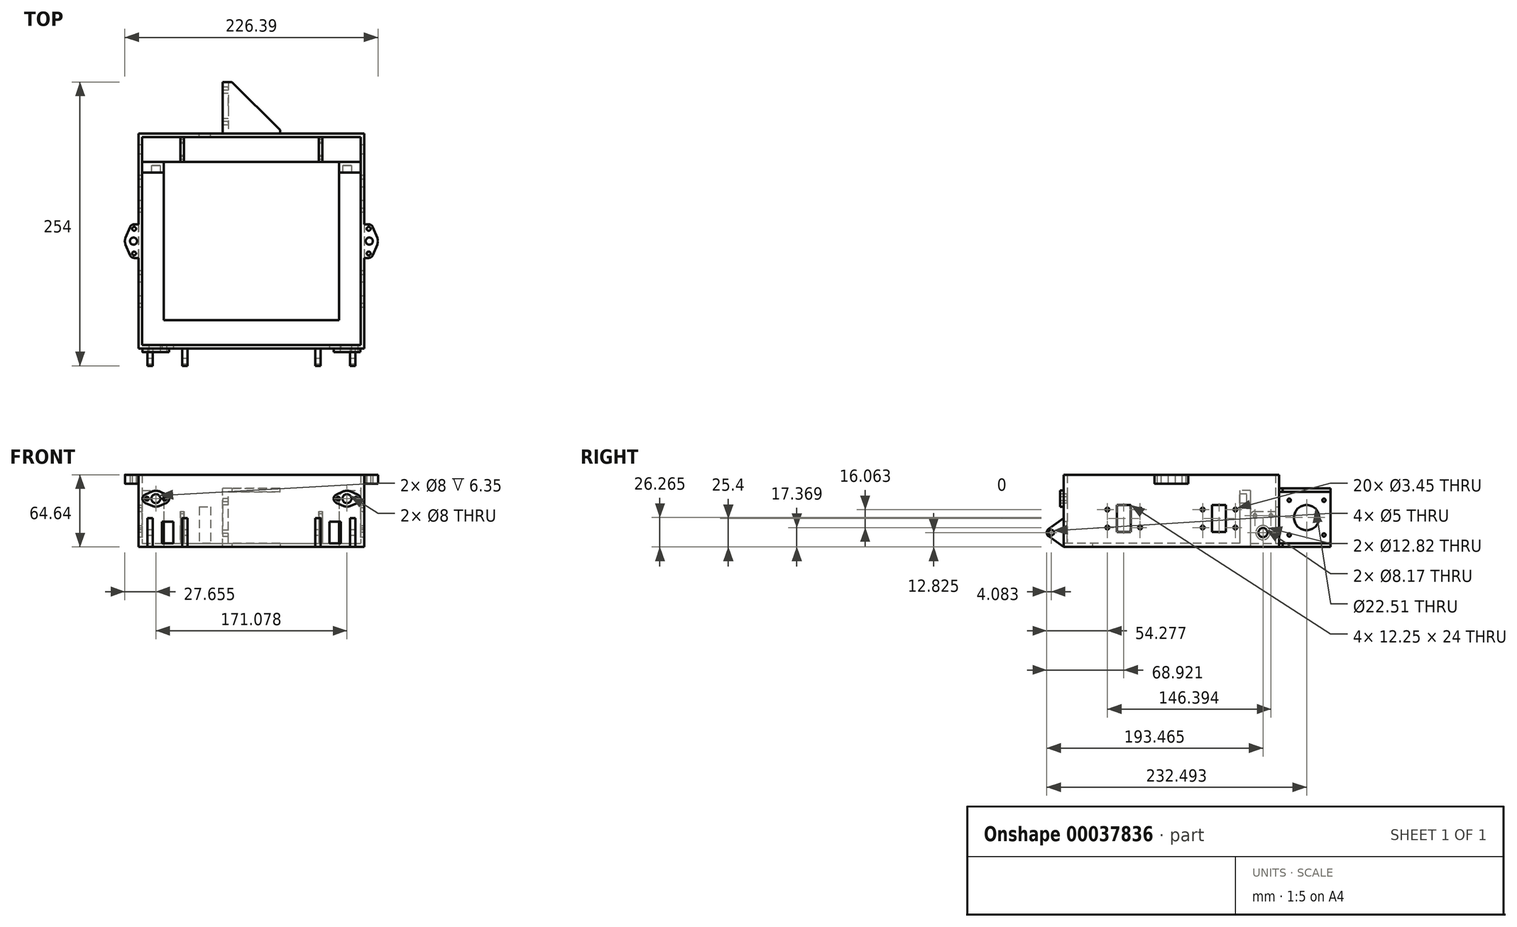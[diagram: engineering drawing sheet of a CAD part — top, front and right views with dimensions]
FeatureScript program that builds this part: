
annotation { "Feature Type Name" : "Feature", "Feature Type Description" : "" }
export const myFeature = defineFeature(function(context is Context, id is Id, definition is map)
    precondition{}
    {
        {
            var Q0;
            Q0=qCreatedBy(makeId("Top.planeOp"),FACE);
            var sketch = newSketch(context, id + "F0", { "sketchPlane" : qUnion([Q0])});
            skLineSegment(sketch, "E0.bottom", {"start": v(0, 0) * mm, "end": v(156.73, 0) * mm});
            skLineSegment(sketch, "E0.top", {"start": v(0, -141.5) * mm, "end": v(156.73, -141.5) * mm});
            skLineSegment(sketch, "E0.left", {"start": v(0, 0) * mm, "end": v(0, -141.5) * mm});
            skLineSegment(sketch, "E0.right", {"start": v(156.73, 0) * mm, "end": v(156.73, -141.5) * mm});
            skLineSegment(sketch, "E1.bottom", {"start": v(-22.61, 25.52) * mm, "end": v(179.34, 25.52) * mm});
            skLineSegment(sketch, "E1.top", {"start": v(-22.61, -167.03) * mm, "end": v(179.34, -167.03) * mm});
            skLineSegment(sketch, "E1.left", {"start": v(-22.61, 25.52) * mm, "end": v(-22.61, -167.03) * mm});
            skLineSegment(sketch, "E1.right", {"start": v(179.34, 25.52) * mm, "end": v(179.34, -167.03) * mm});
            skLineSegment(sketch, "E2", {"start": v(78.36, 0) * mm, "end": v(78.36, 25.52) * mm, "construction": true});
            skLineSegment(sketch, "E3", {"start": v(78.36, -167.03) * mm, "end": v(78.36, -141.5) * mm, "construction": true});
            skSolve(sketch);
        }
        {
            var Q0;
            Q0=qSketchRegion(id+"F0",true);
            extrude(context, id + "F1", {"entities" : qUnion([Q0]), "depth" : 3.17 * mm});
        }
        {
            var Q0;
            Q0=makeQuery(id+"F1.opExtrude","CAP_FACE",FACE,{"disambiguationData":[OSD([sQuery(id+"F0.wireOp",EDGE,"E0.bottom"),sQuery(id+"F0.wireOp",EDGE,"E0.top"),sQuery(id+"F0.wireOp",EDGE,"E0.left"),sQuery(id+"F0.wireOp",EDGE,"E0.right"),sQuery(id+"F0.wireOp",EDGE,"E1.bottom"),sQuery(id+"F0.wireOp",EDGE,"E1.top"),sQuery(id+"F0.wireOp",EDGE,"E1.left"),sQuery(id+"F0.wireOp",EDGE,"E1.right")])],"isStart":false});
            var sketch = newSketch(context, id + "F2", { "sketchPlane" : qUnion([Q0])});
            skLineSegment(sketch, "E4.bottom", {"start": v(-22.61, 25.52) * mm, "end": v(179.34, 25.52) * mm});
            skLineSegment(sketch, "E4.top", {"start": v(-22.61, -167.03) * mm, "end": v(179.34, -167.03) * mm});
            skLineSegment(sketch, "E4.left", {"start": v(-22.61, 25.52) * mm, "end": v(-22.61, -167.03) * mm});
            skLineSegment(sketch, "E4.right", {"start": v(179.34, 25.52) * mm, "end": v(179.34, -167.03) * mm});
            skLineSegment(sketch, "E5", {"start": v(78.36, 0) * mm, "end": v(78.36, -141.5) * mm, "construction": true});
            skLineSegment(sketch, "E6.rect.bottom", {"start": v(-19.44, 22.35) * mm, "end": v(176.17, 22.35) * mm});
            skLineSegment(sketch, "E6.rect.top", {"start": v(-19.44, -163.86) * mm, "end": v(176.17, -163.86) * mm});
            skLineSegment(sketch, "E6.rect.left", {"start": v(-19.44, 22.35) * mm, "end": v(-19.44, -163.86) * mm});
            skLineSegment(sketch, "E6.rect.right", {"start": v(176.17, 22.35) * mm, "end": v(176.17, -163.86) * mm});
            skPoint(sketch, "E6.rect.middle", {"position": v(78.36, -70.75) * mm});
            skLineSegment(sketch, "E7", {"start": v(-19.44, 22.35) * mm, "end": v(-22.61, 22.35) * mm, "construction": true});
            skLineSegment(sketch, "E8", {"start": v(-19.44, 22.35) * mm, "end": v(-19.44, 25.52) * mm, "construction": true});
            skSolve(sketch);
        }
        {
            var Q0;
            Q0=qSketchRegion(id+"F2",true);
            extrude(context, id + "F3", {"entities" : qUnion([Q0]), "operationType" : NewBodyOperationType.ADD, "depth" : 61.46 * mm});
        }
        {
            var Q0;
            Q0=makeQuery(id+"F1.opExtrude","CAP_FACE",FACE,{"disambiguationData":[OSD([sQuery(id+"F0.wireOp",EDGE,"E0.bottom"),sQuery(id+"F0.wireOp",EDGE,"E0.top"),sQuery(id+"F0.wireOp",EDGE,"E0.left"),sQuery(id+"F0.wireOp",EDGE,"E0.right"),sQuery(id+"F0.wireOp",EDGE,"E1.bottom"),sQuery(id+"F0.wireOp",EDGE,"E1.top"),sQuery(id+"F0.wireOp",EDGE,"E1.left"),sQuery(id+"F0.wireOp",EDGE,"E1.right")])],"isStart":false});
            var sketch = newSketch(context, id + "F4", { "sketchPlane" : qUnion([Q0])});
            skLineSegment(sketch, "E9.bottom", {"start": v(-19.44, -9.52) * mm, "end": v(0, -9.52) * mm});
            skLineSegment(sketch, "E9.top", {"start": v(-19.44, 0) * mm, "end": v(0, 0) * mm});
            skLineSegment(sketch, "E9.left", {"start": v(-19.44, -9.53) * mm, "end": v(-19.44, 0) * mm});
            skLineSegment(sketch, "E9.right", {"start": v(0, -9.52) * mm, "end": v(0, 0) * mm});
            skLineSegment(sketch, "E10.bottom", {"start": v(156.73, -9.52) * mm, "end": v(176.17, -9.52) * mm});
            skLineSegment(sketch, "E10.top", {"start": v(156.73, 0) * mm, "end": v(176.17, 0) * mm});
            skLineSegment(sketch, "E10.left", {"start": v(156.73, -9.53) * mm, "end": v(156.73, 0) * mm});
            skLineSegment(sketch, "E10.right", {"start": v(176.17, -9.53) * mm, "end": v(176.17, 0) * mm});
            skSolve(sketch);
        }
        {
            var Q0;
            Q0=qSketchRegion(id+"F4",true);
            var Q1;
            Q1=makeQuery(id+"F3.opExtrude","CAP_FACE",FACE,{"disambiguationData":[OSD([sQuery(id+"F2.wireOp",EDGE,"E4.bottom"),sQuery(id+"F2.wireOp",EDGE,"E4.top"),sQuery(id+"F2.wireOp",EDGE,"E4.left"),sQuery(id+"F2.wireOp",EDGE,"E4.right"),sQuery(id+"F2.wireOp",EDGE,"E6.rect.bottom"),sQuery(id+"F2.wireOp",EDGE,"E6.rect.top"),sQuery(id+"F2.wireOp",EDGE,"E6.rect.left"),sQuery(id+"F2.wireOp",EDGE,"E6.rect.right")])],"isStart":false});
            extrude(context, id + "F5", {"entities" : qUnion([Q0]), "operationType" : NewBodyOperationType.ADD, "endBoundEntityFace" : qUnion([Q1]), "depth" : 47.22 * mm});
        }
        {
            var Q0;
            Q0=makeQuery(id+"F5.opExtrude","SWEPT_FACE",FACE,{"disambiguationData":[OSD([sQuery(id+"F4.wireOp",EDGE,"E9.bottom")])]});
            var sketch = newSketch(context, id + "F6", { "sketchPlane" : qUnion([Q0])});
            skLineSegment(sketch, "E11.bottom", {"start": v(0, 43.22) * mm, "end": v(-7.18, 43.22) * mm, "construction": true});
            skLineSegment(sketch, "E11.right", {"start": v(-7.18, 43.22) * mm, "end": v(-7.18, 50.4) * mm, "construction": true});
            skLineSegment(sketch, "E12", {"start": v(156.73, 43.22) * mm, "end": v(163.9, 43.22) * mm, "construction": true});
            skCircle(sketch, "E13", {"center": v(163.9, 43.22) * mm, "radius": 4 * mm});
            skCircle(sketch, "E14", {"center": v(-7.18, 43.22) * mm, "radius": 4 * mm});
            skSolve(sketch);
        }
        {
            var Q0;
            Q0=qSketchRegion(id+"F6",true);
            extrude(context, id + "F7", {"entities" : qUnion([Q0]), "operationType" : NewBodyOperationType.REMOVE, "oppositeDirection" : true, "depth" : 6.35 * mm});
        }
        {
            var Q0;
            Q0=makeQuery(id+"F5.opExtrude","CAP_EDGE",EDGE,{"disambiguationData":[OSD([sQuery(id+"F4.wireOp",EDGE,"E10.left")])],"isStart":false});
            var Q1;
            Q1=makeQuery(id+"F5.opExtrude","CAP_EDGE",EDGE,{"disambiguationData":[OSD([sQuery(id+"F4.wireOp",EDGE,"E9.right")])],"isStart":false});
            fillet(context, id + "F8", {"entities" : qUnion([Q0, Q1]), "radius" : 7.18 * mm, "tangentPropagation" : true, "allowEdgeOverflow" : false});
        }
        {
            var Q0;
            {var subQ0=sQuery(id+"F0.wireOp",EDGE,"E0.bottom");var subQ1=sQuery(id+"F0.wireOp",EDGE,"E0.right");var subQ2=sQuery(id+"F0.wireOp",EDGE,"E0.left");Q0=makeQuery(id+"F5.boolean.opBoolean","SPLIT",FACE,{"disambiguationData":[TD([makeQuery(id+"F1.opExtrude","SWEPT_FACE",FACE,{"disambiguationData":[OSD([subQ0])]})])],"derivedFrom":makeQuery(id+"F1.opExtrude","CAP_FACE",FACE,{"disambiguationData":[OSD([subQ0,sQuery(id+"F0.wireOp",EDGE,"E0.top"),subQ2,subQ1,sQuery(id+"F0.wireOp",EDGE,"E1.bottom"),sQuery(id+"F0.wireOp",EDGE,"E1.top"),sQuery(id+"F0.wireOp",EDGE,"E1.left"),sQuery(id+"F0.wireOp",EDGE,"E1.right")])],"isStart":false})});}
            var sketch = newSketch(context, id + "F9", { "sketchPlane" : qUnion([Q0])});
            skLineSegment(sketch, "E15.bottom", {"start": v(14.86, 0) * mm, "end": v(18.04, 0) * mm});
            skLineSegment(sketch, "E15.top", {"start": v(14.86, 22.35) * mm, "end": v(18.04, 22.35) * mm});
            skLineSegment(sketch, "E15.left", {"start": v(14.86, 0) * mm, "end": v(14.86, 22.35) * mm});
            skLineSegment(sketch, "E15.right", {"start": v(18.04, 0) * mm, "end": v(18.04, 22.35) * mm});
            skLineSegment(sketch, "E16.bottom", {"start": v(141.86, 0) * mm, "end": v(138.69, 0) * mm});
            skLineSegment(sketch, "E16.top", {"start": v(141.86, 22.35) * mm, "end": v(138.69, 22.35) * mm});
            skLineSegment(sketch, "E16.left", {"start": v(141.86, 0) * mm, "end": v(141.86, 22.35) * mm});
            skLineSegment(sketch, "E16.right", {"start": v(138.69, 0) * mm, "end": v(138.69, 22.35) * mm});
            skLineSegment(sketch, "E17", {"start": v(18.04, 11.17) * mm, "end": v(138.69, 11.17) * mm, "construction": true});
            skLineSegment(sketch, "E18", {"start": v(78.36, 11.17) * mm, "end": v(78.36, 22.35) * mm, "construction": true});
            skSolve(sketch);
        }
        {
            var Q0;
            Q0=qSketchRegion(id+"F9",true);
            extrude(context, id + "F10", {"entities" : qUnion([Q0]), "operationType" : NewBodyOperationType.ADD, "depth" : 28.76 * mm});
        }
        {
            var Q0;
            Q0=makeQuery(id+"F10.opExtrude","SWEPT_FACE",FACE,{"disambiguationData":[OSD([sQuery(id+"F9.wireOp",EDGE,"E15.left")])]});
            var sketch = newSketch(context, id + "F11", { "sketchPlane" : qUnion([Q0])});
            skLineSegment(sketch, "E19", {"start": v(-11.17, 3.18) * mm, "end": v(-11.17, 12.83) * mm, "construction": true});
            skLineSegment(sketch, "E20", {"start": v(-11.17, 12.83) * mm, "end": v(-11.17, 27.97) * mm, "construction": true});
            skLineSegment(sketch, "E21", {"start": v(-18.38, 27.97) * mm, "end": v(-3.97, 27.97) * mm, "construction": true});
            skCircle(sketch, "E22", {"center": v(-11.17, 12.83) * mm, "radius": 6.41 * mm});
            skCircle(sketch, "E23", {"center": v(-18.38, 27.97) * mm, "radius": 1.73 * mm});
            skCircle(sketch, "E24", {"center": v(-3.97, 27.97) * mm, "radius": 1.73 * mm});
            skSolve(sketch);
        }
        {
            var Q0;
            Q0=qSketchRegion(id+"F11",true);
            var Q1;
            Q1=makeQuery(id+"F10.opExtrude","SWEPT_FACE",FACE,{"disambiguationData":[OSD([sQuery(id+"F9.wireOp",EDGE,"E16.left")])]});
            extrude(context, id + "F12", {"entities" : qUnion([Q0]), "operationType" : NewBodyOperationType.REMOVE, "endBound" : BoundingType.UP_TO_SURFACE, "oppositeDirection" : true, "endBoundEntityFace" : qUnion([Q1]), "depth" : 25.4 * mm});
        }
        {
            var Q0;
            Q0=makeQuery(id+"F10.opExtrude","CAP_EDGE",EDGE,{"disambiguationData":[OSD([sQuery(id+"F9.wireOp",EDGE,"E15.bottom")])],"isStart":false});
            var Q1;
            Q1=makeQuery(id+"F10.opExtrude","CAP_EDGE",EDGE,{"disambiguationData":[OSD([sQuery(id+"F9.wireOp",EDGE,"E16.bottom")])],"isStart":false});
            fillet(context, id + "F13", {"entities" : qUnion([Q0, Q1]), "radius" : 3.97 * mm, "tangentPropagation" : true, "allowEdgeOverflow" : false});
        }
        {
            var Q0;
            Q0=makeQuery(id+"F3.boolean.opBoolean","MERGE",FACE,{"derivedFrom":[makeQuery(id+"F1.opExtrude","SWEPT_FACE",FACE,{"disambiguationData":[OSD([sQuery(id+"F0.wireOp",EDGE,"E1.left")])]}),makeQuery(id+"F3.opExtrude","SWEPT_FACE",FACE,{"disambiguationData":[OSD([sQuery(id+"F2.wireOp",EDGE,"E4.left")])]})]});
            var sketch = newSketch(context, id + "F14", { "sketchPlane" : qUnion([Q0])});
            skCircle(sketch, "E25", {"center": v(-11.17, 12.83) * mm, "radius": 4.09 * mm});
            skSolve(sketch);
        }
        {
            var Q0;
            Q0=qSketchRegion(id+"F14",true);
            var Q1;
            Q1=makeQuery(id+"F3.boolean.opBoolean","MERGE",FACE,{"derivedFrom":[makeQuery(id+"F1.opExtrude","SWEPT_FACE",FACE,{"disambiguationData":[OSD([sQuery(id+"F0.wireOp",EDGE,"E1.right")])]}),makeQuery(id+"F3.opExtrude","SWEPT_FACE",FACE,{"disambiguationData":[OSD([sQuery(id+"F2.wireOp",EDGE,"E4.right")])]})]});
            extrude(context, id + "F15", {"entities" : qUnion([Q0]), "operationType" : NewBodyOperationType.REMOVE, "endBound" : BoundingType.UP_TO_SURFACE, "oppositeDirection" : true, "endBoundEntityFace" : qUnion([Q1]), "depth" : 25.4 * mm});
        }
        {
            var Q0;
            Q0=makeQuery(id+"F3.boolean.opBoolean","MERGE",FACE,{"derivedFrom":[makeQuery(id+"F1.opExtrude","SWEPT_FACE",FACE,{"disambiguationData":[OSD([sQuery(id+"F0.wireOp",EDGE,"E1.bottom")])]}),makeQuery(id+"F3.opExtrude","SWEPT_FACE",FACE,{"disambiguationData":[OSD([sQuery(id+"F2.wireOp",EDGE,"E4.bottom")])]})]});
            var sketch = newSketch(context, id + "F16", { "sketchPlane" : qUnion([Q0])});
            skLineSegment(sketch, "E26.bottom", {"start": v(-103.95, 0) * mm, "end": v(-52.77, 0) * mm});
            skLineSegment(sketch, "E26.top", {"start": v(-103.95, 52.53) * mm, "end": v(-52.77, 52.53) * mm});
            skLineSegment(sketch, "E26.right", {"start": v(-52.77, 0) * mm, "end": v(-52.77, 52.53) * mm});
            skLineSegment(sketch, "E27", {"start": v(-52.77, 26.27) * mm, "end": v(-57.77, 26.27) * mm, "construction": true});
            skLineSegment(sketch, "E28", {"start": v(-57.77, 3.18) * mm, "end": v(-57.77, 49.36) * mm});
            skLineSegment(sketch, "E29", {"start": v(-57.77, 3.18) * mm, "end": v(-103.95, 3.18) * mm});
            skLineSegment(sketch, "E30", {"start": v(-103.95, 3.18) * mm, "end": v(-103.95, 0) * mm});
            skLineSegment(sketch, "E31", {"start": v(-57.77, 49.36) * mm, "end": v(-103.95, 49.36) * mm});
            skLineSegment(sketch, "E32", {"start": v(-103.95, 49.36) * mm, "end": v(-103.95, 52.53) * mm});
            skPoint(sketch, "E33", {"position": v(-78.36, 0) * mm});
            skSolve(sketch);
        }
        {
            var Q0;
            Q0=qSketchRegion(id+"F16",true);
            extrude(context, id + "F17", {"entities" : qUnion([Q0]), "operationType" : NewBodyOperationType.ADD, "depth" : 46.18 * mm});
        }
        {
            var Q0;
            Q0=makeQuery(id+"F17.opExtrude","CAP_EDGE",EDGE,{"disambiguationData":[OSD([sQuery(id+"F16.wireOp",EDGE,"E30")])],"isStart":false});
            var Q1;
            Q1=makeQuery(id+"F17.opExtrude","CAP_EDGE",EDGE,{"disambiguationData":[OSD([sQuery(id+"F16.wireOp",EDGE,"E32")])],"isStart":false});
            chamfer(context, id + "F18", {"entities" : qUnion([Q0, Q1]), "width" : 43 * mm, "tangentPropagation" : true});
        }
        {
            var Q0;
            Q0=makeQuery(id+"F17.opExtrude","SWEPT_FACE",FACE,{"disambiguationData":[OSD([sQuery(id+"F16.wireOp",EDGE,"E26.right")])]});
            var sketch = newSketch(context, id + "F19", { "sketchPlane" : qUnion([Q0])});
            skLineSegment(sketch, "E34", {"start": v(-71.7, 26.27) * mm, "end": v(-50.2, 26.27) * mm, "construction": true});
            skLineSegment(sketch, "E35.rect.bottom", {"start": v(-34.7, 10.77) * mm, "end": v(-65.7, 10.77) * mm, "construction": true});
            skLineSegment(sketch, "E35.rect.top", {"start": v(-34.7, 41.77) * mm, "end": v(-65.7, 41.77) * mm, "construction": true});
            skLineSegment(sketch, "E35.rect.left", {"start": v(-34.7, 10.77) * mm, "end": v(-34.7, 41.77) * mm, "construction": true});
            skLineSegment(sketch, "E35.rect.right", {"start": v(-65.7, 10.77) * mm, "end": v(-65.7, 41.77) * mm, "construction": true});
            skPoint(sketch, "E35.rect.middle", {"position": v(-50.2, 26.27) * mm});
            skCircle(sketch, "E36", {"center": v(-50.2, 26.27) * mm, "radius": 11.25 * mm});
            skCircle(sketch, "E37", {"center": v(-34.7, 10.77) * mm, "radius": 1.5 * mm});
            skCircle(sketch, "E38", {"center": v(-65.7, 10.77) * mm, "radius": 1.5 * mm});
            skCircle(sketch, "E39", {"center": v(-65.7, 41.77) * mm, "radius": 1.5 * mm});
            skCircle(sketch, "E40", {"center": v(-34.7, 41.77) * mm, "radius": 1.5 * mm});
            skSolve(sketch);
        }
        {
            var Q0;
            Q0=qSketchRegion(id+"F19",true);
            var Q1;
            Q1=makeQuery(id+"F17.opExtrude","SWEPT_FACE",FACE,{"disambiguationData":[OSD([sQuery(id+"F16.wireOp",EDGE,"E28")])]});
            extrude(context, id + "F20", {"entities" : qUnion([Q0]), "operationType" : NewBodyOperationType.REMOVE, "endBound" : BoundingType.UP_TO_SURFACE, "oppositeDirection" : true, "endBoundEntityFace" : qUnion([Q1]), "depth" : 25.4 * mm});
        }
        {
            var Q0;
            {var subQ1=sQuery(id+"F0.wireOp",EDGE,"E1.left");var subQ2=sQuery(id+"F0.wireOp",EDGE,"E1.bottom");var subQ3=sQuery(id+"F2.wireOp",EDGE,"E4.bottom");Q0=makeQuery(id+"F17.boolean.opBoolean","SPLIT",FACE,{"disambiguationData":[TD([makeQuery(id+"F1.opExtrude","SWEPT_FACE",FACE,{"disambiguationData":[OSD([subQ1])]})])],"derivedFrom":makeQuery(id+"F3.boolean.opBoolean","MERGE",FACE,{"derivedFrom":[makeQuery(id+"F1.opExtrude","SWEPT_FACE",FACE,{"disambiguationData":[OSD([subQ2])]}),makeQuery(id+"F3.opExtrude","SWEPT_FACE",FACE,{"disambiguationData":[OSD([subQ3])]})]})});}
            var sketch = newSketch(context, id + "F21", { "sketchPlane" : qUnion([Q0])});
            skLineSegment(sketch, "E41.bottom", {"start": v(-41.95, 3.18) * mm, "end": v(-31.77, 3.18) * mm});
            skLineSegment(sketch, "E41.top", {"start": v(-41.95, 35.8) * mm, "end": v(-31.77, 35.8) * mm});
            skLineSegment(sketch, "E41.left", {"start": v(-41.95, 3.17) * mm, "end": v(-41.95, 35.8) * mm});
            skLineSegment(sketch, "E41.right", {"start": v(-31.77, 3.18) * mm, "end": v(-31.77, 35.8) * mm});
            skLineSegment(sketch, "E42", {"start": v(-52.77, 26.27) * mm, "end": v(-41.95, 26.27) * mm, "construction": true});
            skLineSegment(sketch, "E43", {"start": v(-41.95, 26.27) * mm, "end": v(-36.86, 26.27) * mm, "construction": true});
            skLineSegment(sketch, "E44", {"start": v(-36.86, 26.27) * mm, "end": v(-36.86, 35.8) * mm, "construction": true});
            skSolve(sketch);
        }
        {
            var Q0;
            Q0=qSketchRegion(id+"F21",true);
            var Q1;
            Q1=makeQuery(id+"FOizmT4TiNgObuU_1.boolean.opBoolean","MERGE",FACE,{"derivedFrom":[makeQuery(id+"F3.opExtrude","SWEPT_FACE",FACE,{"disambiguationData":[OSD([sQuery(id+"F2.wireOp",EDGE,"E6.rect.bottom")])]}),makeQuery(id+"FOizmT4TiNgObuU_1.opExtrude","CAP_FACE",FACE,{"disambiguationData":[OSD([sQuery(id+"F16.wireOp",EDGE,"E26.bottom"),sQuery(id+"F16.wireOp",EDGE,"E26.top"),sQuery(id+"F16.wireOp",EDGE,"E26.right"),sQuery(id+"F16.wireOp",EDGE,"E28"),sQuery(id+"F16.wireOp",EDGE,"E29"),sQuery(id+"F16.wireOp",EDGE,"E30"),sQuery(id+"F16.wireOp",EDGE,"E31"),sQuery(id+"F16.wireOp",EDGE,"E32")])],"isStart":false})]});
            extrude(context, id + "F22", {"entities" : qUnion([Q0]), "operationType" : NewBodyOperationType.REMOVE, "endBound" : BoundingType.UP_TO_SURFACE, "oppositeDirection" : true, "endBoundEntityFace" : qUnion([Q1]), "depth" : 25.4 * mm});
        }
        {
            var Q0;
            Q0=makeQuery(id+"F3.boolean.opBoolean","MERGE",FACE,{"derivedFrom":[makeQuery(id+"F1.opExtrude","SWEPT_FACE",FACE,{"disambiguationData":[OSD([sQuery(id+"F0.wireOp",EDGE,"E1.left")])]}),makeQuery(id+"F3.opExtrude","SWEPT_FACE",FACE,{"disambiguationData":[OSD([sQuery(id+"F2.wireOp",EDGE,"E4.left")])]})]});
            var sketch = newSketch(context, id + "F23", { "sketchPlane" : qUnion([Q0])});
            skLineSegment(sketch, "E45.bottom", {"start": v(85.77, 64.64) * mm, "end": v(55.73, 64.64) * mm});
            skLineSegment(sketch, "E45.top", {"start": v(85.77, 56.7) * mm, "end": v(55.73, 56.7) * mm});
            skLineSegment(sketch, "E45.left", {"start": v(85.77, 64.64) * mm, "end": v(85.77, 56.7) * mm});
            skLineSegment(sketch, "E45.right", {"start": v(55.73, 64.64) * mm, "end": v(55.73, 56.7) * mm});
            skPoint(sketch, "E46", {"position": v(70.75, 64.64) * mm});
            skSolve(sketch);
        }
        {
            var Q0;
            Q0=qSketchRegion(id+"F23",true);
            extrude(context, id + "F24", {"entities" : qUnion([Q0]), "operationType" : NewBodyOperationType.ADD, "depth" : 50.8 * mm});
        }
        {
            var Q0;
            Q0=makeQuery(id+"F3.boolean.opBoolean","MERGE",FACE,{"derivedFrom":[makeQuery(id+"F1.opExtrude","SWEPT_FACE",FACE,{"disambiguationData":[OSD([sQuery(id+"F0.wireOp",EDGE,"E1.top")])]}),makeQuery(id+"F3.opExtrude","SWEPT_FACE",FACE,{"disambiguationData":[OSD([sQuery(id+"F2.wireOp",EDGE,"E4.top")])]})]});
            var sketch = newSketch(context, id + "F25", { "sketchPlane" : qUnion([Q0])});
            skLineSegment(sketch, "E47.bottom", {"start": v(171.43, 0) * mm, "end": v(166.67, 0) * mm});
            skLineSegment(sketch, "E47.top", {"start": v(171.43, 25.65) * mm, "end": v(166.67, 25.65) * mm});
            skLineSegment(sketch, "E47.left", {"start": v(171.43, 0) * mm, "end": v(171.43, 25.65) * mm});
            skLineSegment(sketch, "E47.right", {"start": v(166.67, 0) * mm, "end": v(166.67, 25.65) * mm});
            skLineSegment(sketch, "E48.bottom", {"start": v(135.38, 0) * mm, "end": v(140.14, 0) * mm});
            skLineSegment(sketch, "E48.top", {"start": v(135.38, 25.65) * mm, "end": v(140.14, 25.65) * mm});
            skLineSegment(sketch, "E48.left", {"start": v(135.38, 0) * mm, "end": v(135.38, 25.65) * mm});
            skLineSegment(sketch, "E48.right", {"start": v(140.14, 0) * mm, "end": v(140.14, 25.65) * mm});
            skLineSegment(sketch, "E49.bottom", {"start": v(16.59, 0) * mm, "end": v(21.35, 0) * mm});
            skLineSegment(sketch, "E49.top", {"start": v(16.59, 25.65) * mm, "end": v(21.35, 25.65) * mm});
            skLineSegment(sketch, "E49.left", {"start": v(16.59, 0) * mm, "end": v(16.59, 25.65) * mm});
            skLineSegment(sketch, "E49.right", {"start": v(21.35, 0) * mm, "end": v(21.35, 25.65) * mm});
            skLineSegment(sketch, "E50.bottom", {"start": v(-14.7, 0) * mm, "end": v(-9.94, 0) * mm});
            skLineSegment(sketch, "E50.top", {"start": v(-14.7, 25.65) * mm, "end": v(-9.94, 25.65) * mm});
            skLineSegment(sketch, "E50.left", {"start": v(-14.7, 0) * mm, "end": v(-14.7, 25.65) * mm});
            skLineSegment(sketch, "E50.right", {"start": v(-9.94, 0) * mm, "end": v(-9.94, 25.65) * mm});
            skLineSegment(sketch, "E51", {"start": v(16.59, 12.83) * mm, "end": v(-9.94, 12.83) * mm, "construction": true});
            skLineSegment(sketch, "E52", {"start": v(166.67, 12.83) * mm, "end": v(140.14, 12.83) * mm, "construction": true});
            skPoint(sketch, "E52.endSnap0", {"position": v(166.67, 12.83) * mm});
            skLineSegment(sketch, "E53", {"start": v(171.43, 12.83) * mm, "end": v(179.34, 12.83) * mm, "construction": true});
            skLineSegment(sketch, "E54", {"start": v(-14.7, 12.83) * mm, "end": v(-22.61, 12.83) * mm, "construction": true});
            skPoint(sketch, "E55", {"position": v(153.4, 12.83) * mm});
            skPoint(sketch, "E56", {"position": v(3.32, 12.83) * mm});
            skLineSegment(sketch, "E57", {"start": v(-7.18, 43.22) * mm, "end": v(3.32, 43.22) * mm, "construction": true});
            skLineSegment(sketch, "E58", {"start": v(3.32, 43.22) * mm, "end": v(3.32, 12.83) * mm, "construction": true});
            skSolve(sketch);
        }
        {
            var Q0;
            Q0=qSketchRegion(id+"F25",true);
            extrude(context, id + "F26", {"entities" : qUnion([Q0]), "operationType" : NewBodyOperationType.ADD, "depth" : 25.4 * mm});
        }
        {
            var Q0;
            Q0=makeQuery(id+"F26.opExtrude","SWEPT_FACE",FACE,{"disambiguationData":[OSD([sQuery(id+"F25.wireOp",EDGE,"E50.left")])]});
            var sketch = newSketch(context, id + "F27", { "sketchPlane" : qUnion([Q0])});
            skLineSegment(sketch, "E59", {"start": v(167.03, 12.83) * mm, "end": v(178.2, 12.83) * mm, "construction": true});
            skCircle(sketch, "E60", {"center": v(178.2, 12.83) * mm, "radius": 2.5 * mm});
            skLineSegment(sketch, "E61.bottom", {"start": v(167.03, 0) * mm, "end": v(192.43, 0) * mm});
            skLineSegment(sketch, "E61.top", {"start": v(167.03, 25.65) * mm, "end": v(192.43, 25.65) * mm});
            skLineSegment(sketch, "E61.left", {"start": v(167.03, 0) * mm, "end": v(167.03, 25.65) * mm, "construction": true});
            skLineSegment(sketch, "E61.right", {"start": v(192.43, 0) * mm, "end": v(192.43, 25.65) * mm});
            skLineSegment(sketch, "E62", {"start": v(167.03, 0) * mm, "end": v(180.55, 9.48) * mm});
            skLineSegment(sketch, "E63", {"start": v(167.03, 25.65) * mm, "end": v(180.55, 16.17) * mm});
            skArc(sketch, "E64", {"start": v(180.55, 9.48) * mm, "mid": v(182.3, 12.83) * mm, "end": v(180.55, 16.17) * mm});
            skSolve(sketch);
        }
        {
            var Q0;
            Q0=qSketchRegion(id+"F27",true);
            var Q1;
            Q1=makeQuery(id+"F26.opExtrude","SWEPT_FACE",FACE,{"disambiguationData":[OSD([sQuery(id+"F25.wireOp",EDGE,"E47.left")])]});
            extrude(context, id + "F28", {"entities" : qUnion([Q0]), "operationType" : NewBodyOperationType.REMOVE, "endBound" : BoundingType.UP_TO_SURFACE, "oppositeDirection" : true, "endBoundEntityFace" : qUnion([Q1]), "depth" : 25.4 * mm});
        }
        {
            var Q0;
            Q0=makeQuery(id+"F3.boolean.opBoolean","MERGE",FACE,{"derivedFrom":[makeQuery(id+"F1.opExtrude","SWEPT_FACE",FACE,{"disambiguationData":[OSD([sQuery(id+"F0.wireOp",EDGE,"E1.top")])]}),makeQuery(id+"F3.opExtrude","SWEPT_FACE",FACE,{"disambiguationData":[OSD([sQuery(id+"F2.wireOp",EDGE,"E4.top")])]})]});
            var sketch = newSketch(context, id + "F29", { "sketchPlane" : qUnion([Q0])});
            skLineSegment(sketch, "E65.bottom", {"start": v(158.5, 3.17) * mm, "end": v(148.32, 3.17) * mm});
            skLineSegment(sketch, "E65.top", {"start": v(158.5, 22.48) * mm, "end": v(148.32, 22.48) * mm});
            skLineSegment(sketch, "E65.left", {"start": v(158.5, 3.18) * mm, "end": v(158.5, 22.48) * mm});
            skLineSegment(sketch, "E65.right", {"start": v(148.32, 3.18) * mm, "end": v(148.32, 22.48) * mm});
            skLineSegment(sketch, "E66.bottom", {"start": v(8.41, 3.18) * mm, "end": v(-1.76, 3.18) * mm});
            skLineSegment(sketch, "E66.top", {"start": v(8.41, 22.48) * mm, "end": v(-1.76, 22.48) * mm});
            skLineSegment(sketch, "E66.left", {"start": v(8.41, 3.18) * mm, "end": v(8.41, 22.48) * mm});
            skLineSegment(sketch, "E66.right", {"start": v(-1.76, 3.18) * mm, "end": v(-1.76, 22.48) * mm});
            skLineSegment(sketch, "E67", {"start": v(148.32, 12.83) * mm, "end": v(140.14, 12.83) * mm, "construction": true});
            skLineSegment(sketch, "E68", {"start": v(158.5, 12.83) * mm, "end": v(166.67, 12.83) * mm, "construction": true});
            skLineSegment(sketch, "E69", {"start": v(-1.76, 12.83) * mm, "end": v(-9.94, 12.83) * mm, "construction": true});
            skPoint(sketch, "E69.endSnap0", {"position": v(-1.76, 12.83) * mm});
            skLineSegment(sketch, "E70", {"start": v(8.41, 12.83) * mm, "end": v(16.59, 12.83) * mm, "construction": true});
            skSolve(sketch);
        }
        {
            var Q0;
            Q0=qSketchRegion(id+"F29",true);
            var Q1;
            Q1=makeQuery(id+"F3.opExtrude","SWEPT_FACE",FACE,{"disambiguationData":[OSD([sQuery(id+"F2.wireOp",EDGE,"E6.rect.top")])]});
            extrude(context, id + "F30", {"entities" : qUnion([Q0]), "operationType" : NewBodyOperationType.REMOVE, "endBound" : BoundingType.UP_TO_SURFACE, "oppositeDirection" : true, "endBoundEntityFace" : qUnion([Q1]), "depth" : 25.4 * mm});
        }
        {
            var Q0;
            Q0=makeQuery(id+"F3.boolean.opBoolean","MERGE",FACE,{"derivedFrom":[makeQuery(id+"F1.opExtrude","SWEPT_FACE",FACE,{"disambiguationData":[OSD([sQuery(id+"F0.wireOp",EDGE,"E1.right")])]}),makeQuery(id+"F3.opExtrude","SWEPT_FACE",FACE,{"disambiguationData":[OSD([sQuery(id+"F2.wireOp",EDGE,"E4.right")])]})]});
            var sketch = newSketch(context, id + "F31", { "sketchPlane" : qUnion([Q0])});
            skLineSegment(sketch, "E71.bottom", {"start": v(-55.73, 64.64) * mm, "end": v(-85.77, 64.64) * mm});
            skLineSegment(sketch, "E71.top", {"start": v(-55.73, 56.7) * mm, "end": v(-85.77, 56.7) * mm});
            skLineSegment(sketch, "E71.left", {"start": v(-55.73, 64.64) * mm, "end": v(-55.73, 56.7) * mm});
            skLineSegment(sketch, "E71.right", {"start": v(-85.77, 64.64) * mm, "end": v(-85.77, 56.7) * mm});
            skPoint(sketch, "E72", {"position": v(-70.75, 64.64) * mm});
            skSolve(sketch);
        }
        {
            var Q0;
            Q0=qSketchRegion(id+"F31",true);
            extrude(context, id + "F32", {"entities" : qUnion([Q0]), "operationType" : NewBodyOperationType.ADD, "depth" : 50.8 * mm});
        }
        {
            var Q0;
            Q0=makeQuery(id+"F24.opExtrude","SWEPT_FACE",FACE,{"disambiguationData":[OSD([sQuery(id+"F23.wireOp",EDGE,"E45.top")])]});
            var sketch = newSketch(context, id + "F33", { "sketchPlane" : qUnion([Q0])});
            skLineSegment(sketch, "E73", {"start": v(-22.61, 85.77) * mm, "end": v(-22.61, 55.73) * mm});
            skLineSegment(sketch, "E74", {"start": v(-22.61, 55.73) * mm, "end": v(-26.58, 55.73) * mm});
            skLineSegment(sketch, "E75", {"start": v(-22.61, 85.77) * mm, "end": v(-26.58, 85.77) * mm});
            skLineSegment(sketch, "E76", {"start": v(-22.61, 70.75) * mm, "end": v(-34.83, 70.75) * mm, "construction": true});
            skPoint(sketch, "E76.endSnap0", {"position": v(-22.61, 70.75) * mm});
            skArc(sketch, "E77", {"start": v(-30.25, 58.18) * mm, "mid": v(-28.79, 56.4) * mm, "end": v(-26.58, 55.73) * mm});
            skArc(sketch, "E78", {"start": v(-26.58, 85.77) * mm, "mid": v(-28.79, 85.1) * mm, "end": v(-30.25, 83.33) * mm});
            skArc(sketch, "E79", {"start": v(-34.24, 73.7) * mm, "mid": v(-34.83, 70.75) * mm, "end": v(-34.24, 67.8) * mm});
            skLineSegment(sketch, "E80", {"start": v(-30.25, 58.18) * mm, "end": v(-34.24, 67.8) * mm});
            skLineSegment(sketch, "E81", {"start": v(-30.25, 83.33) * mm, "end": v(-34.24, 73.7) * mm});
            skLineSegment(sketch, "E82.bottom", {"start": v(-26.58, 85.77) * mm, "end": v(-73.41, 85.77) * mm});
            skLineSegment(sketch, "E82.top", {"start": v(-26.58, 55.73) * mm, "end": v(-73.41, 55.73) * mm});
            skLineSegment(sketch, "E82.left", {"start": v(-26.58, 85.77) * mm, "end": v(-26.58, 55.73) * mm, "construction": true});
            skLineSegment(sketch, "E82.right", {"start": v(-73.41, 85.77) * mm, "end": v(-73.41, 55.73) * mm});
            skCircle(sketch, "E83", {"center": v(-26.58, 81.8) * mm, "radius": 1.73 * mm});
            skCircle(sketch, "E84", {"center": v(-27.13, 70.75) * mm, "radius": 3.18 * mm});
            skCircle(sketch, "E85", {"center": v(-26.58, 59.7) * mm, "radius": 1.73 * mm});
            skLineSegment(sketch, "E86.bottom", {"start": v(183.3, 85.77) * mm, "end": v(230.14, 85.77) * mm});
            skLineSegment(sketch, "E86.top", {"start": v(183.3, 55.73) * mm, "end": v(230.14, 55.73) * mm});
            skLineSegment(sketch, "E86.left", {"start": v(183.3, 85.77) * mm, "end": v(183.3, 55.73) * mm, "construction": true});
            skLineSegment(sketch, "E86.right", {"start": v(230.14, 85.77) * mm, "end": v(230.14, 55.73) * mm});
            skLineSegment(sketch, "E87.bottom", {"start": v(179.34, 85.77) * mm, "end": v(183.3, 85.77) * mm});
            skLineSegment(sketch, "E87.top", {"start": v(179.34, 55.73) * mm, "end": v(183.3, 55.73) * mm});
            skLineSegment(sketch, "E87.left", {"start": v(179.34, 85.77) * mm, "end": v(179.34, 55.73) * mm});
            skArc(sketch, "E88", {"start": v(186.97, 83.33) * mm, "mid": v(185.51, 85.1) * mm, "end": v(183.3, 85.77) * mm});
            skArc(sketch, "E89", {"start": v(183.3, 55.73) * mm, "mid": v(185.51, 56.4) * mm, "end": v(186.97, 58.18) * mm});
            skLineSegment(sketch, "E90", {"start": v(186.97, 83.33) * mm, "end": v(190.97, 73.7) * mm});
            skLineSegment(sketch, "E91", {"start": v(186.97, 58.18) * mm, "end": v(190.97, 67.8) * mm});
            skArc(sketch, "E92", {"start": v(190.97, 67.8) * mm, "mid": v(191.56, 70.75) * mm, "end": v(190.97, 73.7) * mm});
            skCircle(sketch, "E93", {"center": v(183.3, 81.8) * mm, "radius": 1.73 * mm});
            skCircle(sketch, "E94", {"center": v(183.86, 70.75) * mm, "radius": 3.18 * mm});
            skCircle(sketch, "E95", {"center": v(183.3, 59.7) * mm, "radius": 1.73 * mm});
            skCircle(sketch, "E96", {"center": v(-27.13, 70.75) * mm, "radius": 4.52 * mm, "construction": true});
            skSolve(sketch);
        }
        {
            var Q0;
            Q0=makeQuery(id+"F33.imprint","IMPRINT",FACE,{"disambiguationData":[TD([[makeQuery(id+"F33.imprint","IMPRINT",EDGE,{"derivedFrom":sQuery(id+"F33.wireOp",EDGE,"E77")}),-1.0]])]});
            var Q1;
            Q1=makeQuery(id+"F33.imprint","IMPRINT",FACE,{"disambiguationData":[TD([[makeQuery(id+"F33.imprint","IMPRINT",EDGE,{"derivedFrom":sQuery(id+"F33.wireOp",EDGE,"E83")}),1.0]])]});
            var Q2;
            Q2=makeQuery(id+"F33.imprint","IMPRINT",FACE,{"disambiguationData":[TD([[makeQuery(id+"F33.imprint","IMPRINT",EDGE,{"derivedFrom":sQuery(id+"F33.wireOp",EDGE,"E84")}),1.0]])]});
            var Q3;
            Q3=makeQuery(id+"F33.imprint","IMPRINT",FACE,{"disambiguationData":[TD([[makeQuery(id+"F33.imprint","IMPRINT",EDGE,{"derivedFrom":sQuery(id+"F33.wireOp",EDGE,"E85")}),1.0]])]});
            var Q4;
            Q4=makeQuery(id+"F33.imprint","IMPRINT",FACE,{"disambiguationData":[TD([[makeQuery(id+"F33.imprint","IMPRINT",EDGE,{"derivedFrom":sQuery(id+"F33.wireOp",EDGE,"E94")}),1.0]])]});
            var Q5;
            Q5=makeQuery(id+"F33.imprint","IMPRINT",FACE,{"disambiguationData":[TD([[makeQuery(id+"F33.imprint","IMPRINT",EDGE,{"derivedFrom":sQuery(id+"F33.wireOp",EDGE,"E86.bottom")}),-1.0]])]});
            var Q6;
            Q6=makeQuery(id+"F33.imprint","IMPRINT",FACE,{"disambiguationData":[TD([[makeQuery(id+"F33.imprint","IMPRINT",EDGE,{"derivedFrom":sQuery(id+"F33.wireOp",EDGE,"E93")}),1.0]])]});
            var Q7;
            Q7=makeQuery(id+"F33.imprint","IMPRINT",FACE,{"disambiguationData":[TD([[makeQuery(id+"F33.imprint","IMPRINT",EDGE,{"derivedFrom":sQuery(id+"F33.wireOp",EDGE,"E95")}),1.0]])]});
            var Q8;
            Q8=makeQuery(id+"F24.boolean.opBoolean","MERGE",FACE,{"derivedFrom":[makeQuery(id+"F5.boolean.opBoolean","MERGE",FACE,{"derivedFrom":[makeQuery(id+"F3.opExtrude","CAP_FACE",FACE,{"disambiguationData":[OSD([sQuery(id+"F2.wireOp",EDGE,"E4.bottom"),sQuery(id+"F2.wireOp",EDGE,"E4.top"),sQuery(id+"F2.wireOp",EDGE,"E4.left"),sQuery(id+"F2.wireOp",EDGE,"E4.right"),sQuery(id+"F2.wireOp",EDGE,"E6.rect.bottom"),sQuery(id+"F2.wireOp",EDGE,"E6.rect.top"),sQuery(id+"F2.wireOp",EDGE,"E6.rect.left"),sQuery(id+"F2.wireOp",EDGE,"E6.rect.right")])],"isStart":false}),makeQuery(id+"F5.opExtrude","CAP_FACE",FACE,{"disambiguationData":[OSD([sQuery(id+"F4.wireOp",EDGE,"E9.bottom"),sQuery(id+"F4.wireOp",EDGE,"E9.top"),sQuery(id+"F4.wireOp",EDGE,"E9.left"),sQuery(id+"F4.wireOp",EDGE,"E9.right")])],"isStart":false}),makeQuery(id+"F5.opExtrude","CAP_FACE",FACE,{"disambiguationData":[OSD([sQuery(id+"F4.wireOp",EDGE,"E10.bottom"),sQuery(id+"F4.wireOp",EDGE,"E10.top"),sQuery(id+"F4.wireOp",EDGE,"E10.left"),sQuery(id+"F4.wireOp",EDGE,"E10.right")])],"isStart":false})]}),makeQuery(id+"F24.opExtrude","SWEPT_FACE",FACE,{"disambiguationData":[OSD([sQuery(id+"F23.wireOp",EDGE,"E45.bottom")])]})]});
            extrude(context, id + "F34", {"entities" : qUnion([Q0, Q1, Q2, Q3, Q4, Q5, Q6, Q7]), "operationType" : NewBodyOperationType.REMOVE, "endBound" : BoundingType.UP_TO_SURFACE, "oppositeDirection" : true, "endBoundEntityFace" : qUnion([Q8]), "depth" : 25.4 * mm});
        }
        {
            var Q0;
            Q0=makeQuery(id+"F3.boolean.opBoolean","MERGE",FACE,{"derivedFrom":[makeQuery(id+"F1.opExtrude","SWEPT_FACE",FACE,{"disambiguationData":[OSD([sQuery(id+"F0.wireOp",EDGE,"E1.right")])]}),makeQuery(id+"F3.opExtrude","SWEPT_FACE",FACE,{"disambiguationData":[OSD([sQuery(id+"F2.wireOp",EDGE,"E4.right")])]})]});
            var sketch = newSketch(context, id + "F35", { "sketchPlane" : qUnion([Q0])});
            skLineSegment(sketch, "E97.rect.bottom", {"start": v(-119.5, 37.4) * mm, "end": v(-107.24, 37.4) * mm});
            skLineSegment(sketch, "E97.rect.top", {"start": v(-119.5, 13.4) * mm, "end": v(-107.24, 13.4) * mm});
            skLineSegment(sketch, "E97.rect.left", {"start": v(-119.5, 37.4) * mm, "end": v(-119.5, 13.4) * mm});
            skLineSegment(sketch, "E97.rect.right", {"start": v(-107.24, 37.4) * mm, "end": v(-107.24, 13.4) * mm});
            skPoint(sketch, "E97.rect.middle", {"position": v(-113.37, 25.4) * mm});
            skLineSegment(sketch, "E98.rect.bottom", {"start": v(-34.26, 13.4) * mm, "end": v(-22.01, 13.4) * mm});
            skLineSegment(sketch, "E98.rect.top", {"start": v(-34.26, 37.4) * mm, "end": v(-22.01, 37.4) * mm});
            skLineSegment(sketch, "E98.rect.left", {"start": v(-34.26, 13.4) * mm, "end": v(-34.26, 37.4) * mm});
            skLineSegment(sketch, "E98.rect.right", {"start": v(-22.01, 13.4) * mm, "end": v(-22.01, 37.4) * mm});
            skPoint(sketch, "E98.rect.middle", {"position": v(-28.14, 25.4) * mm});
            skLineSegment(sketch, "E99", {"start": v(-70.75, 56.7) * mm, "end": v(-70.75, 0) * mm, "construction": true});
            skLineSegment(sketch, "E100", {"start": v(-113.37, 25.4) * mm, "end": v(-28.14, 25.4) * mm, "construction": true});
            skPoint(sketch, "E101", {"position": v(-70.75, 25.4) * mm});
            skLineSegment(sketch, "E102.rect.bottom", {"start": v(-128.01, 33.43) * mm, "end": v(-98.73, 33.43) * mm, "construction": true});
            skLineSegment(sketch, "E102.rect.top", {"start": v(-128.01, 17.37) * mm, "end": v(-98.73, 17.37) * mm, "construction": true});
            skLineSegment(sketch, "E102.rect.left", {"start": v(-128.01, 33.43) * mm, "end": v(-128.01, 17.37) * mm, "construction": true});
            skLineSegment(sketch, "E102.rect.right", {"start": v(-98.73, 33.43) * mm, "end": v(-98.73, 17.37) * mm, "construction": true});
            skLineSegment(sketch, "E103.rect.bottom", {"start": v(-13.5, 33.43) * mm, "end": v(-42.78, 33.43) * mm, "construction": true});
            skLineSegment(sketch, "E103.rect.top", {"start": v(-13.5, 17.37) * mm, "end": v(-42.78, 17.37) * mm, "construction": true});
            skLineSegment(sketch, "E103.rect.left", {"start": v(-13.5, 33.43) * mm, "end": v(-13.5, 17.37) * mm, "construction": true});
            skLineSegment(sketch, "E103.rect.right", {"start": v(-42.78, 33.43) * mm, "end": v(-42.78, 17.37) * mm, "construction": true});
            skCircle(sketch, "E104", {"center": v(-128.01, 33.43) * mm, "radius": 1.73 * mm});
            skCircle(sketch, "E105", {"center": v(-128.01, 17.37) * mm, "radius": 1.73 * mm});
            skCircle(sketch, "E106", {"center": v(-98.73, 17.37) * mm, "radius": 1.73 * mm});
            skCircle(sketch, "E107", {"center": v(-98.73, 33.43) * mm, "radius": 1.73 * mm});
            skCircle(sketch, "E108", {"center": v(-42.78, 33.43) * mm, "radius": 1.73 * mm});
            skCircle(sketch, "E109", {"center": v(-42.78, 17.37) * mm, "radius": 1.73 * mm});
            skCircle(sketch, "E110", {"center": v(-13.5, 17.37) * mm, "radius": 1.73 * mm});
            skCircle(sketch, "E111", {"center": v(-13.5, 33.43) * mm, "radius": 1.73 * mm});
            skCircle(sketch, "E112", {"center": v(-13.5, 33.43) * mm, "radius": 3.97 * mm, "construction": true});
            skSolve(sketch);
        }
        {
            var Q0;
            Q0=qSketchRegion(id+"F35",true);
            var Q1;
            Q1=makeQuery(id+"F3.boolean.opBoolean","MERGE",FACE,{"derivedFrom":[makeQuery(id+"F1.opExtrude","SWEPT_FACE",FACE,{"disambiguationData":[OSD([sQuery(id+"F0.wireOp",EDGE,"E1.left")])]}),makeQuery(id+"F3.opExtrude","SWEPT_FACE",FACE,{"disambiguationData":[OSD([sQuery(id+"F2.wireOp",EDGE,"E4.left")])]})]});
            extrude(context, id + "F36", {"entities" : qUnion([Q0]), "operationType" : NewBodyOperationType.REMOVE, "endBound" : BoundingType.UP_TO_SURFACE, "oppositeDirection" : true, "endBoundEntityFace" : qUnion([Q1]), "depth" : 25.4 * mm});
        }
        {
            var Q0;
            Q0=makeQuery(id+"F1116UBBiX4yyBV_1.boolean.opBoolean","MERGE",FACE,{"derivedFrom":[makeQuery(id+"F3.boolean.opBoolean","MERGE",FACE,{"derivedFrom":[makeQuery(id+"F1.opExtrude","SWEPT_FACE",FACE,{"disambiguationData":[OSD([sQuery(id+"F0.wireOp",EDGE,"E1.top")])]}),makeQuery(id+"F3.opExtrude","SWEPT_FACE",FACE,{"disambiguationData":[OSD([sQuery(id+"F2.wireOp",EDGE,"E4.top")])]})]}),makeQuery(id+"F1116UBBiX4yyBV_1.opExtrude","SWEPT_FACE",FACE,{"disambiguationData":[OSD([sQuery(id+"Fc0i40zSbgQeecz_1.wireOp",EDGE,"a7fb13c4-b29a-4919-afd7-d795112ae47d.top")])]})]});
            var sketch = newSketch(context, id + "F37", { "sketchPlane" : qUnion([Q0])});
            skCircle(sketch, "E113", {"center": v(-7.18, 43.22) * mm, "radius": 4 * mm});
            skCircle(sketch, "E114", {"center": v(163.9, 43.22) * mm, "radius": 4 * mm});
            skSolve(sketch);
        }
        {
            var Q0;
            Q0=qSketchRegion(id+"F37",true);
            var Q1;
            Q1=makeQuery(id+"F3.opExtrude","SWEPT_FACE",FACE,{"disambiguationData":[OSD([sQuery(id+"F2.wireOp",EDGE,"E6.rect.top")])]});
            extrude(context, id + "F38", {"entities" : qUnion([Q0]), "operationType" : NewBodyOperationType.REMOVE, "endBound" : BoundingType.UP_TO_SURFACE, "oppositeDirection" : true, "endBoundEntityFace" : qUnion([Q1]), "depth" : 25.4 * mm});
        }
        {
            var Q0;
            Q0=makeQuery(id+"F3.boolean.opBoolean","MERGE",FACE,{"derivedFrom":[makeQuery(id+"F1.opExtrude","SWEPT_FACE",FACE,{"disambiguationData":[OSD([sQuery(id+"F0.wireOp",EDGE,"E1.top")])]}),makeQuery(id+"F3.opExtrude","SWEPT_FACE",FACE,{"disambiguationData":[OSD([sQuery(id+"F2.wireOp",EDGE,"E4.top")])]})]});
            var sketch = newSketch(context, id + "F39", { "sketchPlane" : qUnion([Q0])});
            skArc(sketch, "E115", {"start": v(173.47, 39.58) * mm, "mid": v(175.84, 43.22) * mm, "end": v(173.47, 46.85) * mm});
            skArc(sketch, "E116", {"start": v(-16.74, 46.85) * mm, "mid": v(-19.11, 43.22) * mm, "end": v(-16.74, 39.58) * mm});
            skArc(sketch, "E117", {"start": v(166.79, 49.78) * mm, "mid": v(163.9, 50.4) * mm, "end": v(161.02, 49.78) * mm});
            skLineSegment(sketch, "E118", {"start": v(166.79, 36.65) * mm, "end": v(173.47, 39.58) * mm});
            skArc(sketch, "E119", {"start": v(161.02, 36.65) * mm, "mid": v(163.9, 36.04) * mm, "end": v(166.79, 36.65) * mm});
            skLineSegment(sketch, "E120", {"start": v(161.02, 49.78) * mm, "end": v(154.34, 46.85) * mm});
            skCircle(sketch, "E121", {"center": v(163.9, 43.22) * mm, "radius": 4 * mm});
            skArc(sketch, "E122", {"start": v(154.34, 46.85) * mm, "mid": v(151.97, 43.22) * mm, "end": v(154.34, 39.58) * mm});
            skLineSegment(sketch, "E123", {"start": v(-16.74, 46.85) * mm, "end": v(-10.06, 49.78) * mm});
            skLineSegment(sketch, "E124", {"start": v(-10.06, 36.65) * mm, "end": v(-16.74, 39.58) * mm});
            skLineSegment(sketch, "E125", {"start": v(166.79, 49.78) * mm, "end": v(173.47, 46.85) * mm});
            skLineSegment(sketch, "E126", {"start": v(161.02, 36.65) * mm, "end": v(154.34, 39.58) * mm});
            skArc(sketch, "E127", {"start": v(-10.06, 36.65) * mm, "mid": v(-7.18, 36.04) * mm, "end": v(-4.29, 36.65) * mm});
            skLineSegment(sketch, "E128", {"start": v(171.87, 43.22) * mm, "end": v(155.93, 43.22) * mm, "construction": true});
            skLineSegment(sketch, "E129", {"start": v(2.4, 39.58) * mm, "end": v(-4.29, 36.65) * mm});
            skLineSegment(sketch, "E130", {"start": v(0.8, 43.22) * mm, "end": v(-15.14, 43.22) * mm, "construction": true});
            skArc(sketch, "E131", {"start": v(2.4, 39.58) * mm, "mid": v(4.76, 43.22) * mm, "end": v(2.4, 46.85) * mm});
            skCircle(sketch, "E132", {"center": v(-7.18, 43.22) * mm, "radius": 4 * mm});
            skArc(sketch, "E133", {"start": v(2.4, 46.85) * mm, "mid": v(-3.18, 43.22) * mm, "end": v(2.4, 39.58) * mm, "construction": true});
            skArc(sketch, "E134", {"start": v(-4.29, 49.78) * mm, "mid": v(-7.18, 50.4) * mm, "end": v(-10.06, 49.78) * mm});
            skLineSegment(sketch, "E135", {"start": v(-4.29, 49.78) * mm, "end": v(2.4, 46.85) * mm});
            skSolve(sketch);
        }
        {
            var Q0;
            Q0=qSketchRegion(id+"F39",true);
            extrude(context, id + "F40", {"entities" : qUnion([Q0]), "operationType" : NewBodyOperationType.ADD, "depth" : 3.17 * mm});
        }
        {
            var Q0;
            Q0=makeQuery(id+"F40.opExtrude","CAP_FACE",FACE,{"disambiguationData":[OSD([sQuery(id+"F39.wireOp",EDGE,"E116"),sQuery(id+"F39.wireOp",EDGE,"E123"),sQuery(id+"F39.wireOp",EDGE,"E124"),sQuery(id+"F39.wireOp",EDGE,"E127"),sQuery(id+"F39.wireOp",EDGE,"E129"),sQuery(id+"F39.wireOp",EDGE,"E131"),sQuery(id+"F39.wireOp",EDGE,"E132"),sQuery(id+"F39.wireOp",EDGE,"E134"),sQuery(id+"F39.wireOp",EDGE,"E135")])],"isStart":false});
            var sketch = newSketch(context, id + "F41", { "sketchPlane" : qUnion([Q0])});
            skCircle(sketch, "E136", {"center": v(0.8, 43.22) * mm, "radius": 1.73 * mm});
            skCircle(sketch, "E137", {"center": v(-15.14, 43.22) * mm, "radius": 1.73 * mm});
            skCircle(sketch, "E138", {"center": v(171.87, 43.22) * mm, "radius": 1.73 * mm});
            skCircle(sketch, "E139", {"center": v(155.93, 43.22) * mm, "radius": 1.73 * mm});
            skSolve(sketch);
        }
        {
            var Q0;
            Q0=qSketchRegion(id+"F41",true);
            var Q1;
            Q1=makeQuery(id+"F3.opExtrude","SWEPT_FACE",FACE,{"disambiguationData":[OSD([sQuery(id+"F2.wireOp",EDGE,"E6.rect.top")])]});
            extrude(context, id + "F42", {"entities" : qUnion([Q0]), "operationType" : NewBodyOperationType.REMOVE, "endBound" : BoundingType.UP_TO_SURFACE, "oppositeDirection" : true, "endBoundEntityFace" : qUnion([Q1]), "depth" : 25.4 * mm});
        }
    });
